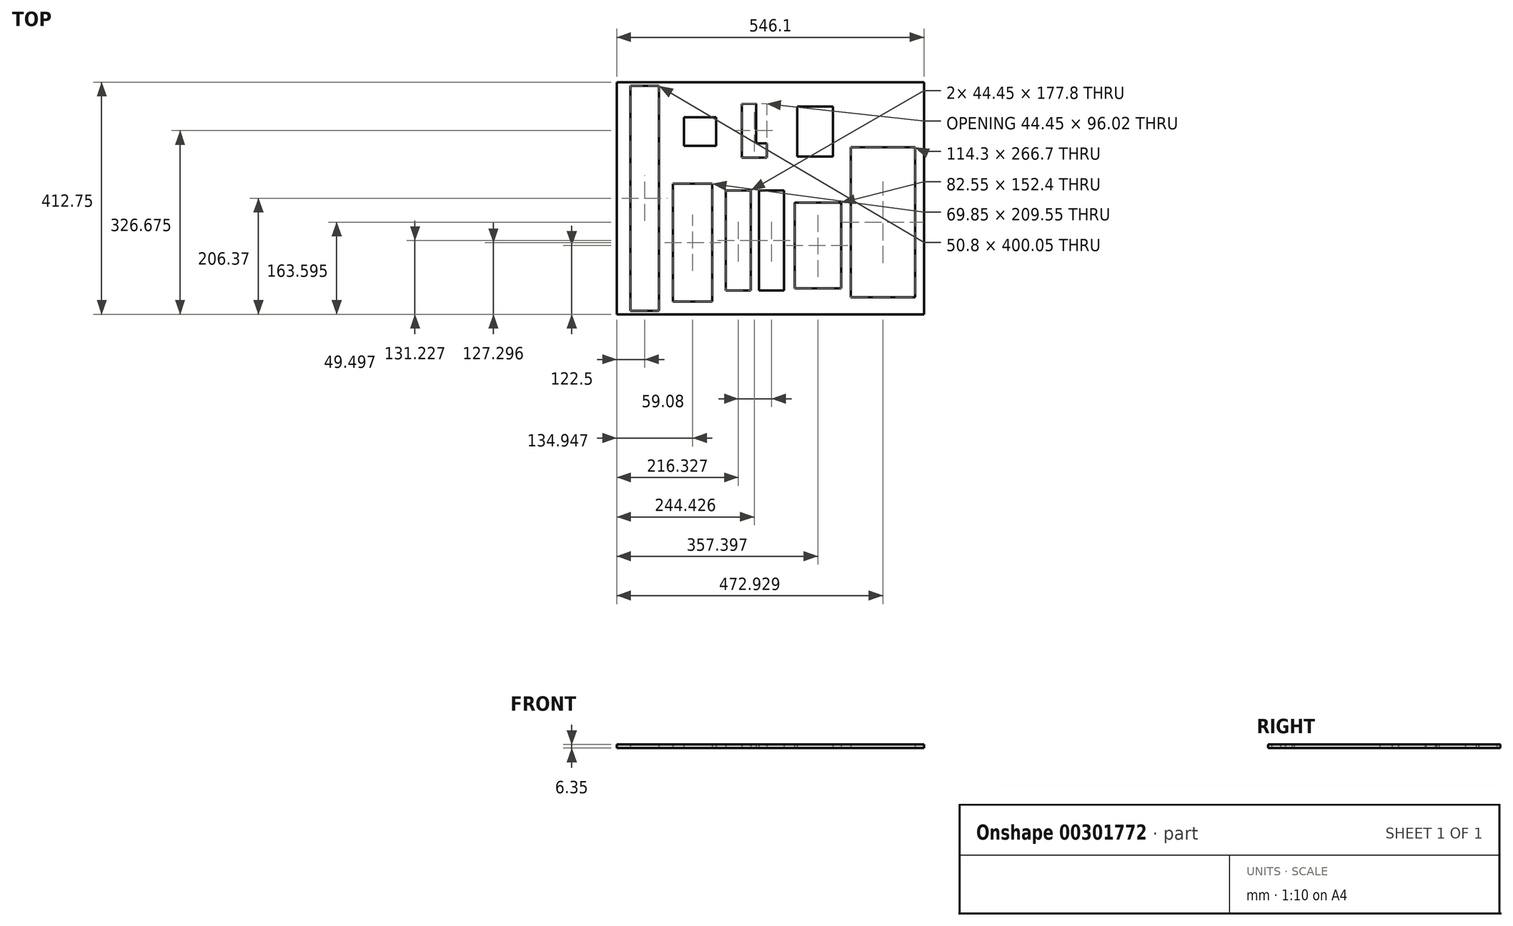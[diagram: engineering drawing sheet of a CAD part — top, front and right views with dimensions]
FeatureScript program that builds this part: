
annotation { "Feature Type Name" : "Feature", "Feature Type Description" : "" }
export const myFeature = defineFeature(function(context is Context, id is Id, definition is map)
    precondition{}
    {
        {
            var Q0;
            Q0=qCreatedBy(makeId("Top.planeOp"),FACE);
            var sketch = newSketch(context, id + "F0", { "sketchPlane" : qUnion([Q0])});
            skLineSegment(sketch, "E0.bottom", {"start": v(-352.19, 207.48) * mm, "end": v(193.91, 207.48) * mm});
            skLineSegment(sketch, "E0.top", {"start": v(-352.19, -205.27) * mm, "end": v(193.91, -205.27) * mm});
            skLineSegment(sketch, "E0.left", {"start": v(-352.19, 207.48) * mm, "end": v(-352.19, -205.27) * mm});
            skLineSegment(sketch, "E0.right", {"start": v(193.91, 207.48) * mm, "end": v(193.91, -205.27) * mm});
            skLineSegment(sketch, "E1.bottom", {"start": v(-328.1, 201.13) * mm, "end": v(-277.3, 201.13) * mm});
            skLineSegment(sketch, "E1.top", {"start": v(-328.1, -198.92) * mm, "end": v(-277.3, -198.92) * mm});
            skLineSegment(sketch, "E1.left", {"start": v(-328.1, 201.13) * mm, "end": v(-328.1, -198.92) * mm});
            skLineSegment(sketch, "E1.right", {"start": v(-277.3, 201.13) * mm, "end": v(-277.3, -198.92) * mm});
            skLineSegment(sketch, "E2.bottom", {"start": v(-252.17, 26.8) * mm, "end": v(-182.32, 26.8) * mm});
            skLineSegment(sketch, "E2.top", {"start": v(-252.17, -182.75) * mm, "end": v(-182.32, -182.75) * mm});
            skLineSegment(sketch, "E2.left", {"start": v(-252.17, 26.8) * mm, "end": v(-252.17, -182.75) * mm});
            skLineSegment(sketch, "E2.right", {"start": v(-182.32, 26.8) * mm, "end": v(-182.32, -182.75) * mm});
            skLineSegment(sketch, "E3.bottom", {"start": v(-158.09, 14.86) * mm, "end": v(-113.64, 14.86) * mm});
            skLineSegment(sketch, "E3.top", {"start": v(-158.09, -162.94) * mm, "end": v(-113.64, -162.94) * mm});
            skLineSegment(sketch, "E3.left", {"start": v(-158.09, 14.86) * mm, "end": v(-158.09, -162.94) * mm});
            skLineSegment(sketch, "E3.right", {"start": v(-113.64, 14.86) * mm, "end": v(-113.64, -162.94) * mm});
            skLineSegment(sketch, "E4.bottom", {"start": v(-99, 14.86) * mm, "end": v(-54.56, 14.86) * mm});
            skLineSegment(sketch, "E4.top", {"start": v(-99, -162.94) * mm, "end": v(-54.56, -162.94) * mm});
            skLineSegment(sketch, "E4.left", {"start": v(-99, 14.86) * mm, "end": v(-99, -162.94) * mm});
            skLineSegment(sketch, "E4.right", {"start": v(-54.56, 14.86) * mm, "end": v(-54.56, -162.94) * mm});
            skLineSegment(sketch, "E5.bottom", {"start": v(-36.07, -6.57) * mm, "end": v(46.48, -6.57) * mm});
            skLineSegment(sketch, "E5.top", {"start": v(-36.07, -158.97) * mm, "end": v(46.48, -158.97) * mm});
            skLineSegment(sketch, "E5.left", {"start": v(-36.07, -6.57) * mm, "end": v(-36.07, -158.97) * mm});
            skLineSegment(sketch, "E5.right", {"start": v(46.48, -6.57) * mm, "end": v(46.48, -158.97) * mm});
            skLineSegment(sketch, "E6.bottom", {"start": v(63.59, 91.68) * mm, "end": v(177.89, 91.68) * mm});
            skLineSegment(sketch, "E6.top", {"start": v(63.59, -175.02) * mm, "end": v(177.89, -175.02) * mm});
            skLineSegment(sketch, "E6.left", {"start": v(63.59, 91.68) * mm, "end": v(63.59, -175.02) * mm});
            skLineSegment(sketch, "E6.right", {"start": v(177.89, 91.68) * mm, "end": v(177.89, -175.02) * mm});
            skLineSegment(sketch, "E7.bottom", {"start": v(-232.5, 145.14) * mm, "end": v(-175.34, 145.14) * mm});
            skLineSegment(sketch, "E7.top", {"start": v(-232.5, 94.34) * mm, "end": v(-175.34, 94.34) * mm});
            skLineSegment(sketch, "E7.left", {"start": v(-232.5, 145.14) * mm, "end": v(-232.5, 94.34) * mm});
            skLineSegment(sketch, "E7.right", {"start": v(-175.34, 145.14) * mm, "end": v(-175.34, 94.34) * mm});
            skLineSegment(sketch, "E8", {"start": v(-129.99, 168.65) * mm, "end": v(-129.99, 73.4) * mm});
            skLineSegment(sketch, "E9", {"start": v(-129.99, 73.4) * mm, "end": v(-85.54, 73.4) * mm});
            skLineSegment(sketch, "E10", {"start": v(-85.54, 73.4) * mm, "end": v(-85.54, 98.8) * mm});
            skLineSegment(sketch, "E11", {"start": v(-85.54, 98.8) * mm, "end": v(-104.6, 98.8) * mm});
            skLineSegment(sketch, "E12", {"start": v(-104.6, 98.8) * mm, "end": v(-104.6, 169.41) * mm});
            skLineSegment(sketch, "E13", {"start": v(-104.6, 169.41) * mm, "end": v(-129.99, 168.65) * mm});
            skLineSegment(sketch, "E14.bottom", {"start": v(-31.63, 164.19) * mm, "end": v(31.87, 164.19) * mm});
            skLineSegment(sketch, "E14.top", {"start": v(-31.63, 75.29) * mm, "end": v(31.87, 75.29) * mm});
            skLineSegment(sketch, "E14.left", {"start": v(-31.63, 164.19) * mm, "end": v(-31.63, 75.29) * mm});
            skLineSegment(sketch, "E14.right", {"start": v(31.87, 164.19) * mm, "end": v(31.87, 75.29) * mm});
            skSolve(sketch);
        }
        {
            var Q0;
            Q0=makeQuery(id+"F0.imprint","IMPRINT",FACE,{"disambiguationData":[TD([[makeQuery(id+"F0.imprint","IMPRINT",EDGE,{"derivedFrom":sQuery(id+"F0.wireOp",EDGE,"E0.bottom")}),-1.0]])]});
            extrude(context, id + "F1", {"entities" : qUnion([Q0]), "depth" : 6.35 * mm});
        }
    });
